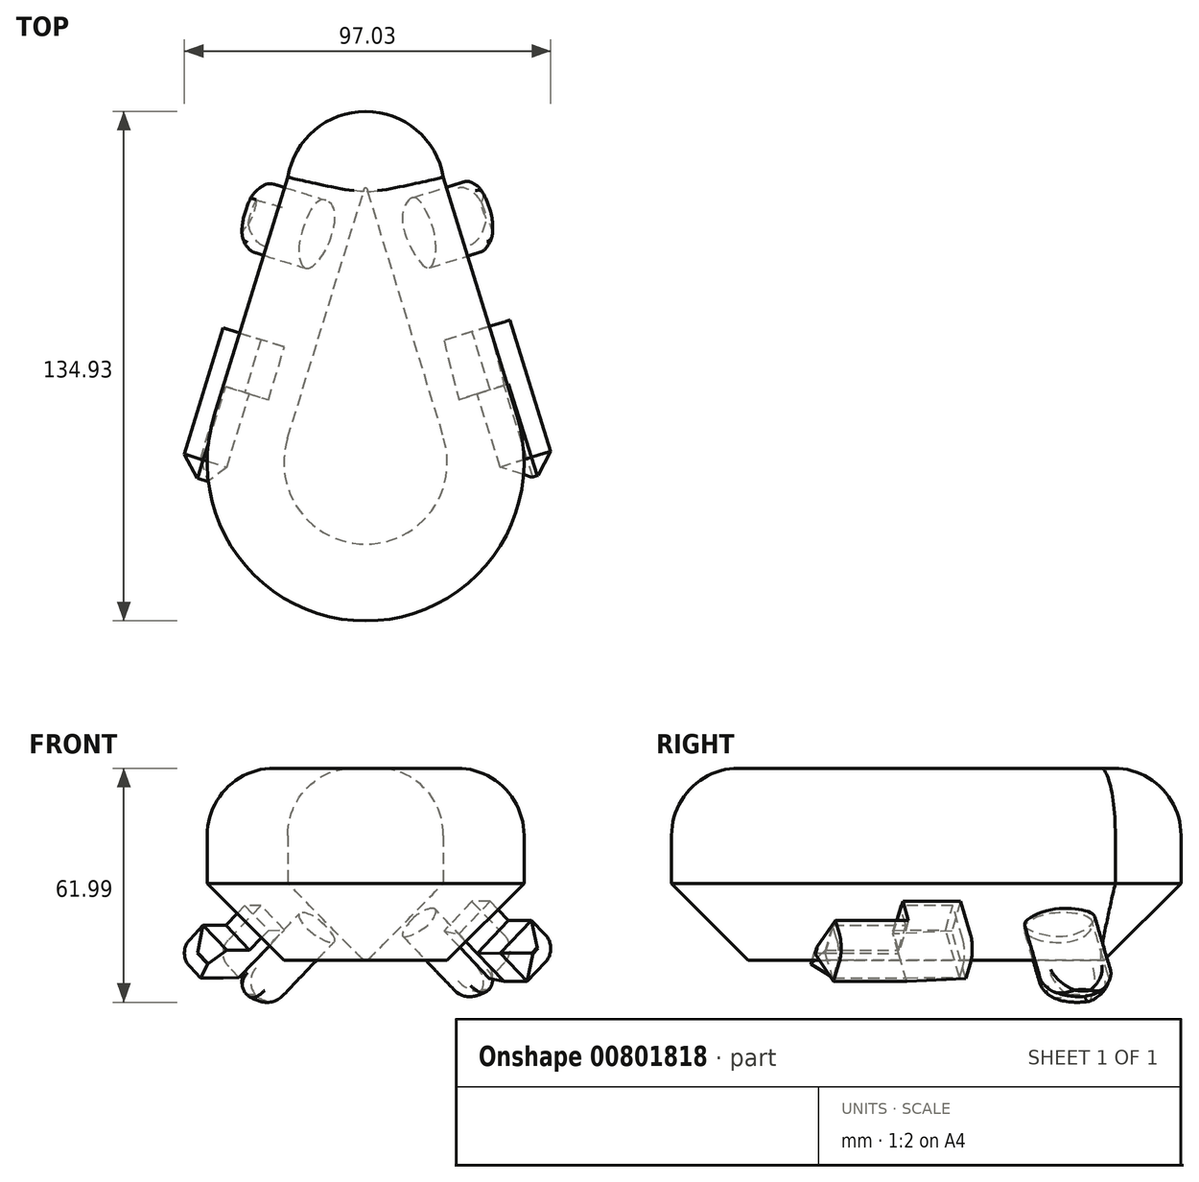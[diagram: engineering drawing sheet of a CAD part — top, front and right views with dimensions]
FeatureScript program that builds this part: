
annotation { "Feature Type Name" : "Feature", "Feature Type Description" : "" }
export const myFeature = defineFeature(function(context is Context, id is Id, definition is map)
    precondition{}
    {
        {
            var Q0;
            Q0=qCreatedBy(makeId("Top.planeOp"),FACE);
            var sketch = newSketch(context, id + "F0", { "sketchPlane" : qUnion([Q0])});
            skArc(sketch, "E0", {"start": v(20.6, 50.24) * mm, "mid": v(0, 67.63) * mm, "end": v(-20.6, 50.24) * mm});
            skArc(sketch, "E1", {"start": v(-40.1, -13) * mm, "mid": v(0, -67.3) * mm, "end": v(40.1, -13) * mm});
            skLineSegment(sketch, "E2", {"start": v(-20.6, 50.24) * mm, "end": v(-40.1, -13) * mm});
            skLineSegment(sketch, "E3", {"start": v(40.1, -13) * mm, "end": v(20.6, 50.24) * mm});
            skSolve(sketch);
        }
        {
            var Q0;
            Q0=makeQuery(id+"F0.imprint","IMPRINT",FACE,{"disambiguationData":[TD([[makeQuery(id+"F0.imprint","IMPRINT",EDGE,{"derivedFrom":sQuery(id+"F0.wireOp",EDGE,"E0")}),1.0]])]});
            extrude(context, id + "F1", {"entities" : qUnion([Q0]), "depth" : 50.8 * mm, "offsetDistance" : 25.4 * mm});
        }
        {
            var Q0;
            Q0=makeQuery(id+"F1.opExtrude","CAP_FACE",FACE,{"disambiguationData":[OSD([sQuery(id+"F0.wireOp",EDGE,"E0"),sQuery(id+"F0.wireOp",EDGE,"E1"),sQuery(id+"F0.wireOp",EDGE,"E2"),sQuery(id+"F0.wireOp",EDGE,"E3")])],"isStart":false});
            fillet(context, id + "F2", {"entities" : qUnion([Q0]), "radius" : 17.78 * mm, "tangentPropagation" : true, "allowEdgeOverflow" : false});
        }
        {
            var Q0;
            Q0=makeQuery(id+"F1.opExtrude","CAP_FACE",FACE,{"disambiguationData":[OSD([sQuery(id+"F0.wireOp",EDGE,"E0"),sQuery(id+"F0.wireOp",EDGE,"E1"),sQuery(id+"F0.wireOp",EDGE,"E2"),sQuery(id+"F0.wireOp",EDGE,"E3")])],"isStart":true});
            chamfer(context, id + "F3", {"entities" : qUnion([Q0]), "width" : 20.32 * mm, "tangentPropagation" : true});
        }
        {
            var Q0;
            Q0=makeQuery(id+"F3.opChamfer","BLEND_FACE",FACE,{"disambiguationData":[OSD([sQuery(id+"F0.wireOp",EDGE,"E2")])]});
            var sketch = newSketch(context, id + "F4", { "sketchPlane" : qUnion([Q0])});
            skFitSpline(sketch, "E4", {"points": [v(-7.4, -28.94) * mm, v(-3.18, -34.31) * mm, v(-2.22, -41.92) * mm, v(-7.33, -45.17) * mm, v(-13.17, -39.1) * mm, v(-14.7, -31.48) * mm, v(-12.14, -27.4) * mm, v(-7.4, -28.94) * mm]});
            skSolve(sketch);
        }
        {
            var Q0;
            Q0 = qSketchRegion(id + "F4", true);
            extrude(context, id + "F5", {"entities" : qUnion([Q0]), "operationType" : NewBodyOperationType.ADD, "depth" : 25.4 * mm, "offsetDistance" : 25.4 * mm});
        }
        {
            var Q0;
            Q0=makeQuery(id+"F3.opChamfer","BLEND_FACE",FACE,{"disambiguationData":[OSD([sQuery(id+"F0.wireOp",EDGE,"E3")])]});
            var sketch = newSketch(context, id + "F6", { "sketchPlane" : qUnion([Q0])});
            skFitSpline(sketch, "E5", {"points": [v(8.08, -46.16) * mm, v(4.27, -41.54) * mm, v(6.14, -33.4) * mm, v(13.47, -27.8) * mm, v(16.01, -35.01) * mm, v(12.15, -43.82) * mm, v(8.08, -46.16) * mm]});
            skSolve(sketch);
        }
        {
            var Q0;
            Q0=makeQuery(id+"F6.imprint","IMPRINT",FACE,{"disambiguationData":[TD([[makeQuery(id+"F6.imprint","IMPRINT",EDGE,{"derivedFrom":sQuery(id+"F6.wireOp",EDGE,"E5")}),-1.0]])]});
            extrude(context, id + "F7", {"entities" : qUnion([Q0]), "operationType" : NewBodyOperationType.ADD, "depth" : 25.4 * mm, "offsetDistance" : 25.4 * mm});
        }
        {
            var Q0;
            Q0=makeQuery(id+"F7.opExtrude","CAP_EDGE",EDGE,{"disambiguationData":[OSD([sQuery(id+"F6.wireOp",EDGE,"E5")])],"isStart":false});
            fillet(context, id + "F8", {"entities" : qUnion([Q0]), "radius" : 5.08 * mm, "tangentPropagation" : true, "allowEdgeOverflow" : false});
        }
        {
            var Q0;
            Q0=makeQuery(id+"F5.opExtrude","CAP_FACE",FACE,{"disambiguationData":[OSD([sQuery(id+"F4.wireOp",EDGE,"E4")])],"isStart":false});
            fillet(context, id + "F9", {"entities" : qUnion([Q0]), "radius" : 5.08 * mm, "tangentPropagation" : true, "allowEdgeOverflow" : false});
        }
        {
            var Q0;
            Q0=makeQuery(id+"F3.opChamfer","BLEND_FACE",FACE,{"disambiguationData":[OSD([sQuery(id+"F0.wireOp",EDGE,"E2")])]});
            var sketch = newSketch(context, id + "F10", { "sketchPlane" : qUnion([Q0])});
            skLineSegment(sketch, "E6", {"start": v(-19.96, -7.32) * mm, "end": v(-28.39, -11) * mm});
            skLineSegment(sketch, "E7", {"start": v(-28.39, -11) * mm, "end": v(-34.24, 2.43) * mm});
            skLineSegment(sketch, "E8", {"start": v(-34.24, 2.43) * mm, "end": v(-25.73, 6.14) * mm});
            skLineSegment(sketch, "E9", {"start": v(-25.73, 6.14) * mm, "end": v(-19.96, -7.32) * mm});
            skSolve(sketch);
        }
        {
            var Q0;
            Q0 = qSketchRegion(id + "F10", true);
            extrude(context, id + "F11", {"entities" : qUnion([Q0]), "operationType" : NewBodyOperationType.ADD, "depth" : 17.78 * mm, "offsetDistance" : 25.4 * mm});
        }
        {
            var Q0;
            Q0=makeQuery(id+"F3.opChamfer","BLEND_FACE",FACE,{"disambiguationData":[OSD([sQuery(id+"F0.wireOp",EDGE,"E3")])]});
            var sketch = newSketch(context, id + "F12", { "sketchPlane" : qUnion([Q0])});
            skLineSegment(sketch, "E10", {"start": v(24.3, 6.38) * mm, "end": v(35.56, 1.4) * mm});
            skLineSegment(sketch, "E11", {"start": v(35.56, 1.4) * mm, "end": v(29.07, -13.28) * mm});
            skLineSegment(sketch, "E12", {"start": v(29.07, -13.28) * mm, "end": v(18.97, -8.82) * mm});
            skLineSegment(sketch, "E13", {"start": v(18.97, -8.82) * mm, "end": v(24.3, 6.38) * mm});
            skSolve(sketch);
        }
        {
            var Q0;
            Q0 = qSketchRegion(id + "F12", true);
            extrude(context, id + "F13", {"entities" : qUnion([Q0]), "operationType" : NewBodyOperationType.ADD, "depth" : 17.78 * mm, "offsetDistance" : 25.4 * mm});
        }
        {
            var Q0;
            Q0=makeQuery(id+"F11.opExtrude","SWEPT_FACE",FACE,{"disambiguationData":[OSD([sQuery(id+"F10.wireOp",EDGE,"E8")])]});
            var sketch = newSketch(context, id + "F14", { "sketchPlane" : qUnion([Q0])});
            skLineSegment(sketch, "E14", {"start": v(-41.16, 1.85) * mm, "end": v(-34.6, -4.71) * mm});
            skLineSegment(sketch, "E15", {"start": v(-34.6, -4.71) * mm, "end": v(-27.3, 2.59) * mm});
            skLineSegment(sketch, "E16", {"start": v(-27.3, 2.59) * mm, "end": v(-33.86, 9.15) * mm});
            skLineSegment(sketch, "E17", {"start": v(-33.86, 9.15) * mm, "end": v(-41.16, 1.85) * mm});
            skSolve(sketch);
        }
        {
            var Q0;
            Q0 = qSketchRegion(id + "F14", true);
            extrude(context, id + "F15", {"entities" : qUnion([Q0]), "operationType" : NewBodyOperationType.ADD, "depth" : 25.4 * mm, "offsetDistance" : 25.4 * mm});
        }
        {
            var Q0;
            Q0=makeQuery(id+"F13.opExtrude","SWEPT_FACE",FACE,{"disambiguationData":[OSD([sQuery(id+"F12.wireOp",EDGE,"E10")])]});
            var sketch = newSketch(context, id + "F16", { "sketchPlane" : qUnion([Q0])});
            skLineSegment(sketch, "E18", {"start": v(33.56, -5.72) * mm, "end": v(42.25, 2.99) * mm});
            skPoint(sketch, "E19.end.orphan", {"position": v(35.96, 9.27) * mm});
            skPoint(sketch, "E20.start.orphan", {"position": v(27.27, 0.56) * mm});
            skLineSegment(sketch, "E21", {"start": v(42.25, 2.99) * mm, "end": v(34.78, 10.44) * mm});
            skLineSegment(sketch, "E22", {"start": v(34.78, 10.44) * mm, "end": v(26.1, 1.73) * mm});
            skLineSegment(sketch, "E23", {"start": v(26.1, 1.73) * mm, "end": v(33.56, -5.72) * mm});
            skSolve(sketch);
        }
        {
            var Q0;
            Q0 = qSketchRegion(id + "F16", true);
            extrude(context, id + "F17", {"entities" : qUnion([Q0]), "operationType" : NewBodyOperationType.ADD, "depth" : 25.4 * mm, "offsetDistance" : 25.4 * mm});
        }
        {
            var Q0;
            Q0=makeQuery(id+"F15.boolean.opBoolean","MERGE",EDGE,{"derivedFrom":[makeQuery(id+"F11.opExtrude","CAP_EDGE",EDGE,{"disambiguationData":[OSD([sQuery(id+"F10.wireOp",EDGE,"E7")])],"isStart":false}),makeQuery(id+"F15.opExtrude","SWEPT_EDGE",EDGE,{"disambiguationData":[OSD([sQuery(id+"F14.wireOp",EDGE,"E14"),sQuery(id+"F14.wireOp",EDGE,"E17")])]})]});
            fillet(context, id + "F18", {"entities" : qUnion([Q0]), "radius" : 5.08 * mm, "tangentPropagation" : true, "allowEdgeOverflow" : false});
        }
        {
            var Q0;
            Q0=makeQuery(id+"F17.boolean.opBoolean","MERGE",EDGE,{"derivedFrom":[makeQuery(id+"F13.opExtrude","CAP_EDGE",EDGE,{"disambiguationData":[OSD([sQuery(id+"F12.wireOp",EDGE,"E11")])],"isStart":false}),makeQuery(id+"F17.opExtrude","SWEPT_EDGE",EDGE,{"disambiguationData":[OSD([sQuery(id+"F16.wireOp",EDGE,"E18"),sQuery(id+"F16.wireOp",EDGE,"E21")])]})]});
            fillet(context, id + "F19", {"entities" : qUnion([Q0]), "radius" : 5.08 * mm, "tangentPropagation" : true, "allowEdgeOverflow" : false});
        }
        {
            var Q0;
            Q0=makeQuery(id+"F17.opExtrude","CAP_FACE",FACE,{"disambiguationData":[OSD([sQuery(id+"F16.wireOp",EDGE,"E18"),sQuery(id+"F16.wireOp",EDGE,"E21"),sQuery(id+"F16.wireOp",EDGE,"E22"),sQuery(id+"F16.wireOp",EDGE,"E23")])],"isStart":false});
            chamfer(context, id + "F20", {"entities" : qUnion([Q0]), "width" : 5.08 * mm, "tangentPropagation" : true});
        }
        {
            var Q0;
            {var subQ0=sQuery(id+"F14.wireOp",EDGE,"E17");var subQ1=sQuery(id+"F14.wireOp",EDGE,"E14");Q0=makeQuery(id+"F18.opFillet","BLEND_EDGE",EDGE,{"blendedFrom":[makeQuery(id+"F15.boolean.opBoolean","MERGE",EDGE,{"derivedFrom":[makeQuery(id+"F11.opExtrude","CAP_EDGE",EDGE,{"disambiguationData":[OSD([sQuery(id+"F10.wireOp",EDGE,"E7")])],"isStart":false}),makeQuery(id+"F15.opExtrude","SWEPT_EDGE",EDGE,{"disambiguationData":[OSD([subQ1,subQ0])]})]}),makeQuery(id+"F15.opExtrude","CAP_FACE",FACE,{"disambiguationData":[OSD([subQ1,sQuery(id+"F14.wireOp",EDGE,"E15"),sQuery(id+"F14.wireOp",EDGE,"E16"),subQ0])],"isStart":false})],"blendedInto":[makeQuery(id+"F15.opExtrude","CAP_FACE",FACE,{"disambiguationData":[OSD([subQ1,sQuery(id+"F14.wireOp",EDGE,"E15"),sQuery(id+"F14.wireOp",EDGE,"E16"),subQ0])],"isStart":false})]});}
            var Q1;
            Q1=makeQuery(id+"F15.opExtrude","CAP_EDGE",EDGE,{"disambiguationData":[OSD([sQuery(id+"F14.wireOp",EDGE,"E16")])],"isStart":false});
            chamfer(context, id + "F21", {"entities" : qUnion([Q0, Q1]), "width" : 5.08 * mm, "tangentPropagation" : true});
        }
    });
